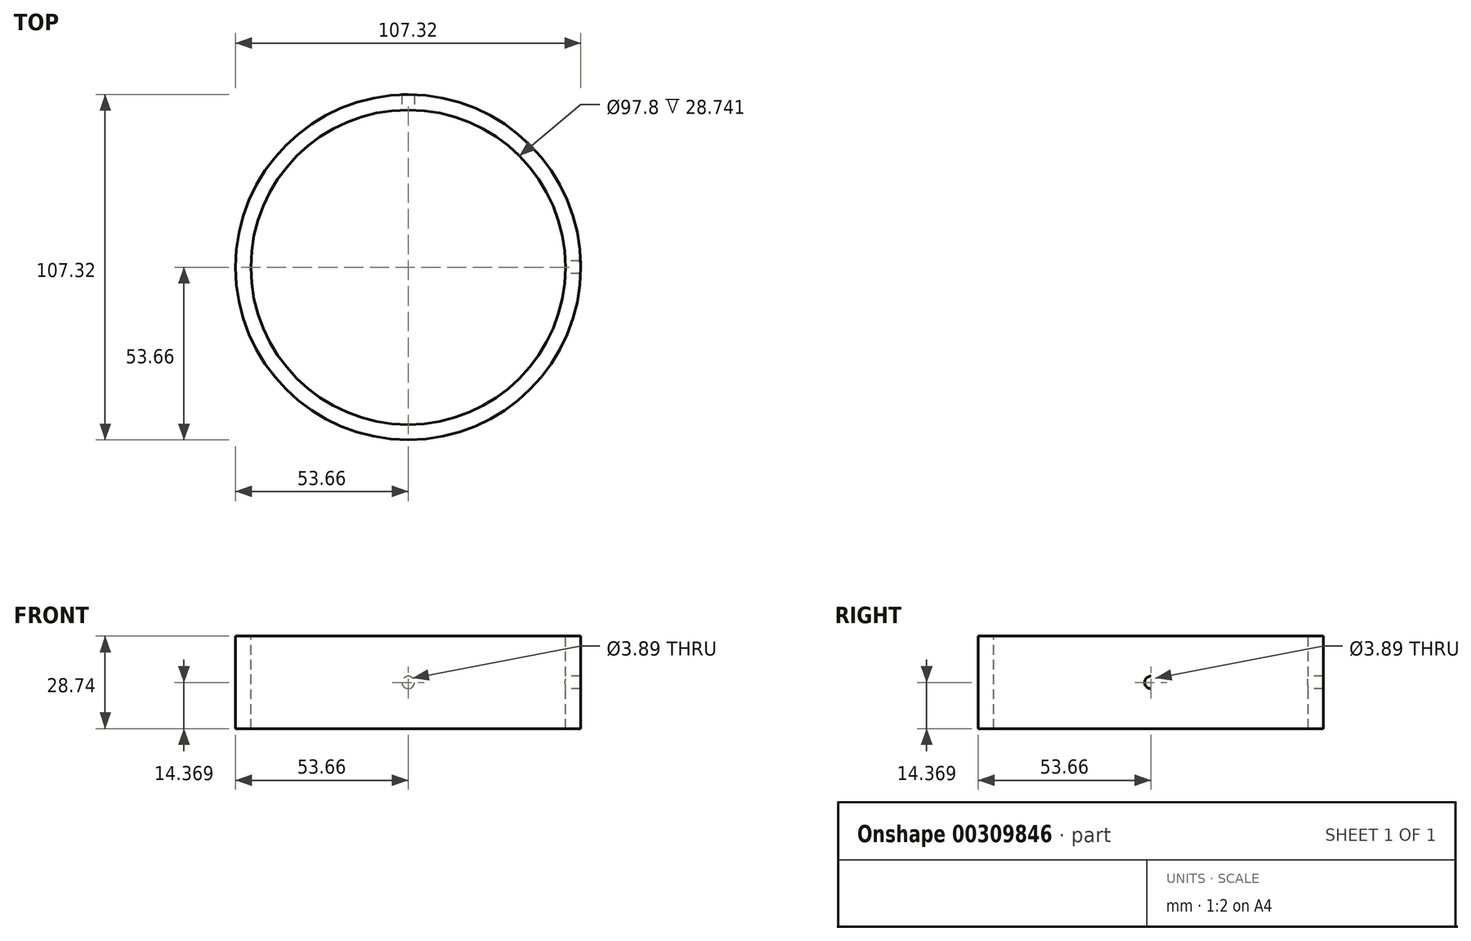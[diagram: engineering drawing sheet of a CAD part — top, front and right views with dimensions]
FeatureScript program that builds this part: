
annotation { "Feature Type Name" : "Feature", "Feature Type Description" : "" }
export const myFeature = defineFeature(function(context is Context, id is Id, definition is map)
    precondition{}
    {
        {
            var Q0;
            Q0=qCreatedBy(makeId("Right.planeOp"),FACE);
            var sketch = newSketch(context, id + "F0", { "sketchPlane" : qUnion([Q0])});
            skLineSegment(sketch, "E0.bottom", {"start": v(0, 0) * mm, "end": v(53.65, 0) * mm});
            skLineSegment(sketch, "E0.top", {"start": v(0, -28.74) * mm, "end": v(53.66, -28.74) * mm});
            skLineSegment(sketch, "E0.left", {"start": v(0, 0) * mm, "end": v(0, -28.74) * mm});
            skLineSegment(sketch, "E0.right", {"start": v(53.66, 0) * mm, "end": v(53.66, -28.74) * mm});
            skSolve(sketch);
        }
        {
            var Q0;
            Q0=qCreatedBy(makeId("Front.planeOp"),FACE);
            var sketch = newSketch(context, id + "F1", { "sketchPlane" : qUnion([Q0])});
            skLineSegment(sketch, "E1.bottom", {"start": v(0, 0) * mm, "end": v(48.9, 0) * mm});
            skLineSegment(sketch, "E1.top", {"start": v(0, -28.74) * mm, "end": v(48.9, -28.74) * mm});
            skLineSegment(sketch, "E1.left", {"start": v(0, 0) * mm, "end": v(0, -28.74) * mm});
            skLineSegment(sketch, "E1.right", {"start": v(48.9, 0) * mm, "end": v(48.9, -28.74) * mm});
            skSolve(sketch);
        }
        {
            var Q0;
            Q0=qCreatedBy(makeId("Right.planeOp"),FACE);
            var sketch = newSketch(context, id + "F2", { "sketchPlane" : qUnion([Q0])});
            skPoint(sketch, "E2", {"position": v(0, 0) * mm});
            skPoint(sketch, "E3", {"position": v(0, -14.37) * mm});
            skSolve(sketch);
        }
        {
            var Q0;
            Q0=qCreatedBy(makeId("Front.planeOp"),FACE);
            var sketch = newSketch(context, id + "F3", { "sketchPlane" : qUnion([Q0])});
            skPoint(sketch, "E4", {"position": v(0, -14.37) * mm});
            skSolve(sketch);
        }
        {
            var Q0;
            Q0=makeQuery(id+"F0.imprint","IMPRINT",FACE,{"disambiguationData":[TD([[makeQuery(id+"F0.imprint","IMPRINT",EDGE,{"derivedFrom":sQuery(id+"F0.wireOp",EDGE,"E0.bottom")}),-1.0]])]});
            var Q1;
            Q1=sQuery(id+"F0.wireOp",EDGE,"E0.left");
            revolve(context, id + "F4", {"entities" : qUnion([Q0]), "axis" : qUnion([Q1]), "revolveType" : RevolveType.FULL});
        }
        {
            var Q0;
            Q0=makeQuery(id+"F1.imprint","IMPRINT",FACE,{"disambiguationData":[TD([[makeQuery(id+"F1.imprint","IMPRINT",EDGE,{"derivedFrom":sQuery(id+"F1.wireOp",EDGE,"E1.bottom")}),-1.0]])]});
            var Q1;
            Q1=sQuery(id+"F1.wireOp",EDGE,"E1.left");
            revolve(context, id + "F5", {"operationType" : NewBodyOperationType.REMOVE, "entities" : qUnion([Q0]), "axis" : qUnion([Q1]), "revolveType" : RevolveType.FULL});
        }
        {
            var Q0;
            Q0=sQuery(id+"F2.wireOp",VERTEX,"E3");
            var Q1;
            Q1=makeQuery(id+"F4.opRevolve","SWEPT_BODY",BODY,{"disambiguationData":[OSD([sQuery(id+"F0.wireOp",EDGE,"E0.bottom"),sQuery(id+"F0.wireOp",EDGE,"E0.top"),sQuery(id+"F0.wireOp",EDGE,"E0.left"),sQuery(id+"F0.wireOp",EDGE,"E0.right")])]});
            hole(context, id + "F6", {"style" : HoleStyle.SIMPLE, "endStyle" : HoleEndStyle.THROUGH, "oppositeDirection" : true, "holeDiameter" : 3.9 * mm, "tappedDepth" : 12.7 * mm, "tapClearance" : 3, "locations" : qUnion([Q0]), "scope" : qUnion([Q1])});
        }
        {
            var Q0;
            Q0=sQuery(id+"F3.wireOp",VERTEX,"E4");
            var Q1;
            Q1=makeQuery(id+"F4.opRevolve","SWEPT_BODY",BODY,{"disambiguationData":[OSD([sQuery(id+"F0.wireOp",EDGE,"E0.bottom"),sQuery(id+"F0.wireOp",EDGE,"E0.top"),sQuery(id+"F0.wireOp",EDGE,"E0.left"),sQuery(id+"F0.wireOp",EDGE,"E0.right")])]});
            hole(context, id + "F7", {"style" : HoleStyle.SIMPLE, "endStyle" : HoleEndStyle.THROUGH, "holeDiameter" : 3.9 * mm, "tappedDepth" : 12.7 * mm, "tapClearance" : 3, "locations" : qUnion([Q0]), "scope" : qUnion([Q1])});
        }
    });
